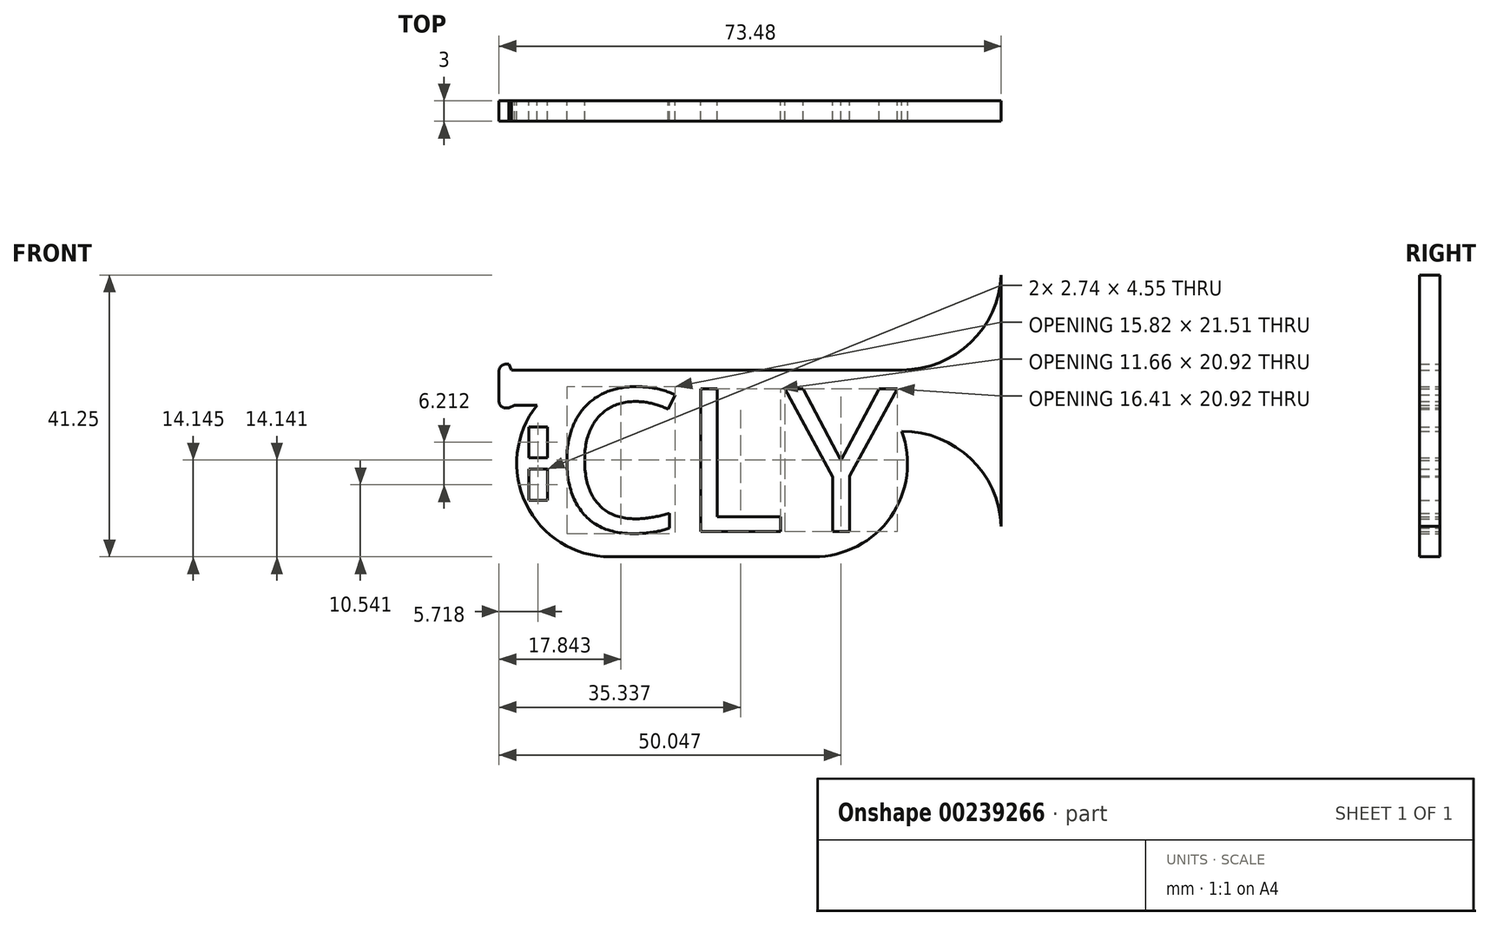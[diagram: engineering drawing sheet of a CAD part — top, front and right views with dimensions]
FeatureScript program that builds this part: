
annotation { "Feature Type Name" : "Feature", "Feature Type Description" : "" }
export const myFeature = defineFeature(function(context is Context, id is Id, definition is map)
    precondition{}
    {
        {
            var Q0;
            Q0=qCreatedBy(makeId("Front.planeOp"),FACE);
            var sketch = newSketch(context, id + "F0", { "sketchPlane" : qUnion([Q0])});
            skArc(sketch, "E0", {"start": v(-10.7, 8.5) * mm, "mid": v(-12.3, -5.95) * mm, "end": v(0, -13.67) * mm});
            skArc(sketch, "E1", {"start": v(29.83, -13.67) * mm, "mid": v(41.04, -7.82) * mm, "end": v(42.66, 4.72) * mm});
            skLineSegment(sketch, "E2", {"start": v(0, 13.67) * mm, "end": v(29.83, 13.67) * mm});
            skLineSegment(sketch, "E3", {"start": v(0, -13.67) * mm, "end": v(29.83, -13.67) * mm});
            skLineSegment(sketch, "E4", {"start": v(0, 13.67) * mm, "end": v(-14.43, 13.67) * mm});
            skLineSegment(sketch, "E5", {"start": v(-14.43, 13.67) * mm, "end": v(-14.83, 14.51) * mm});
            skLineSegment(sketch, "E6", {"start": v(-14.83, 14.51) * mm, "end": v(-15.27, 14.51) * mm});
            skLineSegment(sketch, "E7", {"start": v(-16.27, 13.51) * mm, "end": v(-16.27, 9.1) * mm});
            skLineSegment(sketch, "E8", {"start": v(-15.27, 8.1) * mm, "end": v(-14.83, 8.1) * mm});
            skLineSegment(sketch, "E9", {"start": v(-14.83, 8.1) * mm, "end": v(-13.99, 8.5) * mm});
            skLineSegment(sketch, "E10", {"start": v(-13.99, 8.5) * mm, "end": v(-10.7, 8.5) * mm});
            skPoint(sketch, "E11.visualSharp", {"position": v(-16.27, 14.51) * mm});
            skArc(sketch, "E11.filletArc", {"start": v(-15.27, 14.51) * mm, "mid": v(-15.98, 14.22) * mm, "end": v(-16.27, 13.51) * mm});
            skPoint(sketch, "E12.visualSharp", {"position": v(-16.27, 8.1) * mm});
            skArc(sketch, "E12.filletArc", {"start": v(-16.27, 9.1) * mm, "mid": v(-15.98, 8.4) * mm, "end": v(-15.27, 8.1) * mm});
            skLineSegment(sketch, "E13", {"start": v(29.83, 13.67) * mm, "end": v(42.66, 13.67) * mm});
            skLineSegment(sketch, "E14", {"start": v(42.66, 4.72) * mm, "end": v(42.66, 4.72) * mm});
            skLineSegment(sketch, "E15", {"start": v(42.66, 13.67) * mm, "end": v(42.66, 4.72) * mm, "construction": true});
            skArc(sketch, "E16", {"start": v(42.66, 13.67) * mm, "mid": v(53.19, 18.17) * mm, "end": v(57.21, 28.88) * mm});
            skArc(sketch, "E17", {"start": v(57.21, -9.2) * mm, "mid": v(52.73, 0.68) * mm, "end": v(42.66, 4.72) * mm});
            skLineSegment(sketch, "E18", {"start": v(42.66, 28.23) * mm, "end": v(42.66, -9.84) * mm, "construction": true});
            skLineSegment(sketch, "E19", {"start": v(57.21, 28.88) * mm, "end": v(57.21, -9.2) * mm});
            skLineSegment(sketch, "E20.bottom", {"start": v(-11.92, 5.36) * mm, "end": v(-9.18, 5.36) * mm});
            skLineSegment(sketch, "E20.top", {"start": v(-11.92, -5.4) * mm, "end": v(-9.18, -5.4) * mm});
            skLineSegment(sketch, "E20.left", {"start": v(-11.92, 5.36) * mm, "end": v(-11.92, 0.8) * mm});
            skLineSegment(sketch, "E20.right", {"start": v(-9.18, 5.36) * mm, "end": v(-9.18, 0.8) * mm});
            skPoint(sketch, "E21.endSnap0", {"position": v(-9.18, -0.02) * mm});
            skLineSegment(sketch, "E22.trimOffspring", {"start": v(-11.92, -0.86) * mm, "end": v(-11.92, -5.4) * mm});
            skLineSegment(sketch, "E23.trimOffspring", {"start": v(-9.18, -0.86) * mm, "end": v(-9.18, -5.4) * mm});
            skLineSegment(sketch, "E24", {"start": v(-11.92, 0.8) * mm, "end": v(-9.18, 0.8) * mm});
            skLineSegment(sketch, "E25", {"start": v(-11.92, -0.86) * mm, "end": v(-9.18, -0.86) * mm});
            skPoint(sketch, "E26.orphan", {"position": v(-9.18, 0) * mm});
            skPoint(sketch, "E27.orphan", {"position": v(-11.92, -0.02) * mm});
            skText(sketch, "E28", { "text": "CLY", "fontName": "OpenSans-Regular.ttf"});
            const initialGuessF0  = {"E28": [-0.00813, -0.00999, 1, 0, 0.0211]};
            skSetInitialGuess(sketch, initialGuessF0);
            skSolve(sketch);
        }
        {
            var Q0;
            Q0=makeQuery(id+"F0.imprint","IMPRINT",FACE,{"disambiguationData":[TD([[makeQuery(id+"F0.imprint","IMPRINT",EDGE,{"derivedFrom":sQuery(id+"F0.wireOp",EDGE,"E0")}),1.0]])]});
            extrude(context, id + "F1", {"entities" : qUnion([Q0]), "depth" : 3 * mm});
        }
    });
